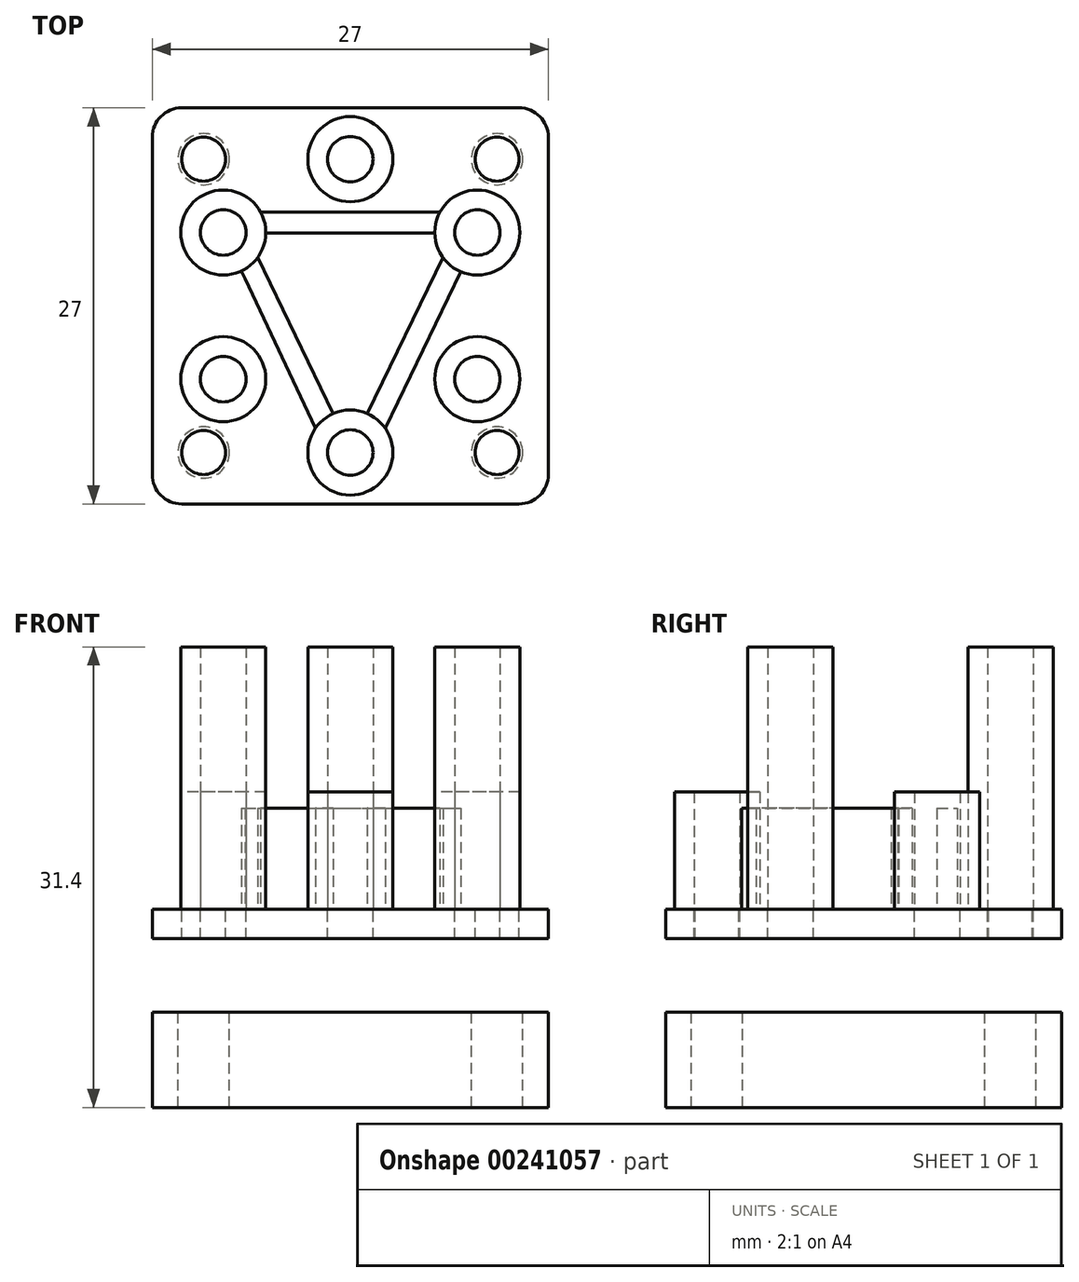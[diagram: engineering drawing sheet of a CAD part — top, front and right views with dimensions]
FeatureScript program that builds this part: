
annotation { "Feature Type Name" : "Feature", "Feature Type Description" : "" }
export const myFeature = defineFeature(function(context is Context, id is Id, definition is map)
    precondition{}
    {
        {
            var Q0;
            Q0=qCreatedBy(makeId("Top.planeOp"),FACE);
            var sketch = newSketch(context, id + "F0", { "sketchPlane" : qUnion([Q0])});
            skLineSegment(sketch, "E0.bottom", {"start": v(-13.5, 13.5) * mm, "end": v(13.5, 13.5) * mm});
            skLineSegment(sketch, "E0.top", {"start": v(-13.5, -13.5) * mm, "end": v(13.5, -13.5) * mm});
            skLineSegment(sketch, "E0.left", {"start": v(-13.5, 13.5) * mm, "end": v(-13.5, -13.5) * mm});
            skLineSegment(sketch, "E0.right", {"start": v(13.5, 13.5) * mm, "end": v(13.5, -13.5) * mm});
            skPoint(sketch, "E1", {"position": v(0, 13.5) * mm});
            skPoint(sketch, "E2", {"position": v(-13.5, 0) * mm});
            skSolve(sketch);
        }
        {
            var Q0;
            Q0=makeQuery(id+"F0.imprint","IMPRINT",FACE,{"disambiguationData":[TD([[makeQuery(id+"F0.imprint","IMPRINT",EDGE,{"derivedFrom":sQuery(id+"F0.wireOp",EDGE,"E0.bottom")}),-1.0]])]});
            extrude(context, id + "F1", {"entities" : qUnion([Q0]), "depth" : 2 * mm});
        }
        {
            var Q0;
            Q0=makeQuery(id+"F1.opExtrude","CAP_FACE",FACE,{"disambiguationData":[OSD([sQuery(id+"F0.wireOp",EDGE,"E0.bottom"),sQuery(id+"F0.wireOp",EDGE,"E0.top"),sQuery(id+"F0.wireOp",EDGE,"E0.left"),sQuery(id+"F0.wireOp",EDGE,"E0.right")])],"isStart":false});
            var sketch = newSketch(context, id + "F2", { "sketchPlane" : qUnion([Q0])});
            skPoint(sketch, "E3", {"position": v(0, 13.5) * mm});
            skPoint(sketch, "E4", {"position": v(-10, 10) * mm});
            skPoint(sketch, "E5", {"position": v(10, 10) * mm});
            skPoint(sketch, "E6", {"position": v(10, -10) * mm});
            skPoint(sketch, "E7", {"position": v(-10, -10) * mm});
            skLineSegment(sketch, "E8", {"start": v(-13.5, 13.5) * mm, "end": v(-10, 13.5) * mm});
            skPoint(sketch, "E9.endSnap0", {"position": v(-11.75, 13.5) * mm});
            skLineSegment(sketch, "E10", {"start": v(-13.5, 13.5) * mm, "end": v(-13.5, 10) * mm});
            skLineSegment(sketch, "E11", {"start": v(13.5, -13.5) * mm, "end": v(13.5, -10) * mm});
            skLineSegment(sketch, "E12", {"start": v(13.5, -13.5) * mm, "end": v(10, -13.5) * mm});
            skCircle(sketch, "E13", {"center": v(-10, 10) * mm, "radius": 1.5 * mm});
            skCircle(sketch, "E14", {"center": v(10, 10) * mm, "radius": 1.5 * mm});
            skCircle(sketch, "E15", {"center": v(-10, -10) * mm, "radius": 1.5 * mm});
            skCircle(sketch, "E16", {"center": v(10, -10) * mm, "radius": 1.5 * mm});
            skLineSegment(sketch, "E17", {"start": v(-10, 10) * mm, "end": v(-10, -10) * mm, "construction": true});
            skLineSegment(sketch, "E18", {"start": v(10, 10) * mm, "end": v(-10, 10) * mm, "construction": true});
            skPoint(sketch, "E19", {"position": v(0, 10) * mm});
            skPoint(sketch, "E20", {"position": v(-10, 0) * mm});
            skSolve(sketch);
        }
        {
            var Q0;
            Q0=makeQuery(id+"F2.imprint","IMPRINT",FACE,{"disambiguationData":[TD([[makeQuery(id+"F2.imprint","IMPRINT",EDGE,{"derivedFrom":sQuery(id+"F2.wireOp",EDGE,"E13")}),1.0]])]});
            var Q1;
            Q1=makeQuery(id+"F2.imprint","IMPRINT",FACE,{"disambiguationData":[TD([[makeQuery(id+"F2.imprint","IMPRINT",EDGE,{"derivedFrom":sQuery(id+"F2.wireOp",EDGE,"E14")}),1.0]])]});
            var Q2;
            Q2=makeQuery(id+"F2.imprint","IMPRINT",FACE,{"disambiguationData":[TD([[makeQuery(id+"F2.imprint","IMPRINT",EDGE,{"derivedFrom":sQuery(id+"F2.wireOp",EDGE,"E16")}),1.0]])]});
            var Q3;
            Q3=makeQuery(id+"F2.imprint","IMPRINT",FACE,{"disambiguationData":[TD([[makeQuery(id+"F2.imprint","IMPRINT",EDGE,{"derivedFrom":sQuery(id+"F2.wireOp",EDGE,"E15")}),1.0]])]});
            extrude(context, id + "F3", {"entities" : qUnion([Q0, Q1, Q2, Q3]), "operationType" : NewBodyOperationType.REMOVE, "oppositeDirection" : true, "depth" : 5 * mm});
        }
        {
            var Q0;
            Q0=makeQuery(id+"F1.opExtrude","SWEPT_EDGE",EDGE,{"disambiguationData":[OSD([sQuery(id+"F0.wireOp",EDGE,"E0.top"),sQuery(id+"F0.wireOp",EDGE,"E0.right")])]});
            var Q1;
            Q1=makeQuery(id+"F1.opExtrude","SWEPT_EDGE",EDGE,{"disambiguationData":[OSD([sQuery(id+"F0.wireOp",EDGE,"E0.bottom"),sQuery(id+"F0.wireOp",EDGE,"E0.left")])]});
            var Q2;
            Q2=makeQuery(id+"F1.opExtrude","SWEPT_EDGE",EDGE,{"disambiguationData":[OSD([sQuery(id+"F0.wireOp",EDGE,"E0.bottom"),sQuery(id+"F0.wireOp",EDGE,"E0.right")])]});
            var Q3;
            Q3=makeQuery(id+"F1.opExtrude","SWEPT_EDGE",EDGE,{"disambiguationData":[OSD([sQuery(id+"F0.wireOp",EDGE,"E0.top"),sQuery(id+"F0.wireOp",EDGE,"E0.left")])]});
            fillet(context, id + "F4", {"entities" : qUnion([Q0, Q1, Q2, Q3]), "radius" : 2 * mm, "tangentPropagation" : true, "allowEdgeOverflow" : false});
        }
        {
            var Q0;
            Q0=makeQuery(id+"F1.opExtrude","CAP_FACE",FACE,{"disambiguationData":[OSD([sQuery(id+"F0.wireOp",EDGE,"E0.bottom"),sQuery(id+"F0.wireOp",EDGE,"E0.top"),sQuery(id+"F0.wireOp",EDGE,"E0.left"),sQuery(id+"F0.wireOp",EDGE,"E0.right")])],"isStart":true});
            var sketch = newSketch(context, id + "F5", { "sketchPlane" : qUnion([Q0])});
            skPoint(sketch, "E21", {"position": v(0, 0) * mm});
            skSolve(sketch);
        }
        {
            var Q0;
            Q0=makeQuery(id+"F1.opExtrude","CAP_FACE",FACE,{"disambiguationData":[OSD([sQuery(id+"F0.wireOp",EDGE,"E0.bottom"),sQuery(id+"F0.wireOp",EDGE,"E0.top"),sQuery(id+"F0.wireOp",EDGE,"E0.left"),sQuery(id+"F0.wireOp",EDGE,"E0.right")])],"isStart":false});
            var sketch = newSketch(context, id + "F6", { "sketchPlane" : qUnion([Q0])});
            skCircle(sketch, "E22.cCircle", {"center": v(0, 0) * mm, "radius": 8.66 * mm, "construction": true});
            skLineSegment(sketch, "E22.0", {"start": v(0, -10) * mm, "end": v(-8.66, -5) * mm});
            skLineSegment(sketch, "E22.1", {"start": v(-8.66, -5) * mm, "end": v(-8.66, 5) * mm});
            skLineSegment(sketch, "E22.2", {"start": v(-8.66, 5) * mm, "end": v(0, 10) * mm});
            skLineSegment(sketch, "E22.3", {"start": v(0, 10) * mm, "end": v(8.66, 5) * mm});
            skLineSegment(sketch, "E22.4", {"start": v(8.66, 5) * mm, "end": v(8.66, -5) * mm});
            skLineSegment(sketch, "E22.5", {"start": v(8.66, -5) * mm, "end": v(0, -10) * mm});
            skPoint(sketch, "E22.0.midPoint", {"position": v(-4.33, -7.5) * mm});
            skPoint(sketch, "E23", {"position": v(0, 10) * mm});
            skPoint(sketch, "E24", {"position": v(0, -10) * mm});
            skPoint(sketch, "E25", {"position": v(-8.66, 0) * mm});
            skCircle(sketch, "E26", {"center": v(0, 10) * mm, "radius": 1.55 * mm});
            skCircle(sketch, "E27", {"center": v(-8.66, -5) * mm, "radius": 1.55 * mm});
            skCircle(sketch, "E28", {"center": v(8.66, -5) * mm, "radius": 1.55 * mm});
            skCircle(sketch, "E29", {"center": v(-8.66, 5) * mm, "radius": 1.55 * mm});
            skCircle(sketch, "E30", {"center": v(8.66, 5) * mm, "radius": 1.55 * mm});
            skCircle(sketch, "E31", {"center": v(0, -10) * mm, "radius": 1.55 * mm});
            skCircle(sketch, "E32", {"center": v(-8.66, 5) * mm, "radius": 2.9 * mm});
            skCircle(sketch, "E33", {"center": v(-8.66, -5) * mm, "radius": 2.9 * mm});
            skCircle(sketch, "E34", {"center": v(0, -10) * mm, "radius": 2.9 * mm});
            skCircle(sketch, "E35", {"center": v(8.66, -5) * mm, "radius": 2.9 * mm});
            skCircle(sketch, "E36", {"center": v(8.66, 5) * mm, "radius": 2.9 * mm});
            skCircle(sketch, "E37", {"center": v(0, 10) * mm, "radius": 2.9 * mm});
            skPoint(sketch, "E38", {"position": v(-5.76, 4.98) * mm});
            skPoint(sketch, "E39", {"position": v(5.76, 4.98) * mm});
            skPoint(sketch, "E40", {"position": v(46.87, -20.06) * mm});
            skLineSegment(sketch, "E41", {"start": v(-5.76, 4.98) * mm, "end": v(5.76, 4.98) * mm});
            skPoint(sketch, "E42", {"position": v(-1.16, -7.34) * mm});
            skPoint(sketch, "E43", {"position": v(1.16, -7.34) * mm});
            skPoint(sketch, "E44", {"position": v(-6.3, 3.3) * mm});
            skPoint(sketch, "E45", {"position": v(6.3, 3.3) * mm});
            skLineSegment(sketch, "E46", {"start": v(-6.3, 3.3) * mm, "end": v(-1.16, -7.34) * mm});
            skLineSegment(sketch, "E47", {"start": v(1.16, -7.34) * mm, "end": v(6.3, 3.3) * mm});
            skPoint(sketch, "E48", {"position": v(-7.43, 2.37) * mm});
            skLineSegment(sketch, "E49", {"start": v(-7.43, 2.37) * mm, "end": v(-7.18, 1.86) * mm});
            skLineSegment(sketch, "E50", {"start": v(-7.18, 1.86) * mm, "end": v(-2.39, -8.35) * mm});
            skLineSegment(sketch, "E51", {"start": v(0, 6.38) * mm, "end": v(6.1, 6.38) * mm});
            skLineSegment(sketch, "E52", {"start": v(0, 6.38) * mm, "end": v(-6.1, 6.38) * mm});
            skPoint(sketch, "E53", {"position": v(2.37, -8.33) * mm});
            skLineSegment(sketch, "E54", {"start": v(2.37, -8.33) * mm, "end": v(7.53, 2.33) * mm});
            skSolve(sketch);
        }
        {
            var Q0;
            {var subQ0=sQuery(id+"F6.wireOp",EDGE,"E37");var subQ1=sQuery(id+"F6.wireOp",EDGE,"E22.2");var subQ2=makeQuery(id+"F6.imprint","INTERSECT",VERTEX,{"derivedFrom":[subQ1,subQ0]});Q0=makeQuery(id+"F6.imprint","IMPRINT",FACE,{"disambiguationData":[TD([[makeQuery(id+"F6.imprint","IMPRINT",EDGE,{"disambiguationData":[TD([[subQ2,-1.0]])],"derivedFrom":subQ1}),1.0]])]});}
            var Q1;
            {var subQ0=sQuery(id+"F6.wireOp",EDGE,"E37");var subQ1=sQuery(id+"F6.wireOp",EDGE,"E22.2");var subQ2=makeQuery(id+"F6.imprint","INTERSECT",VERTEX,{"derivedFrom":[subQ1,subQ0]});Q1=makeQuery(id+"F6.imprint","IMPRINT",FACE,{"disambiguationData":[TD([[makeQuery(id+"F6.imprint","IMPRINT",EDGE,{"disambiguationData":[TD([[subQ2,-1.0]])],"derivedFrom":subQ1}),-1.0]])]});}
            var Q2;
            {var subQ0=sQuery(id+"F6.wireOp",EDGE,"E35");var subQ1=sQuery(id+"F6.wireOp",EDGE,"E22.4");var subQ2=makeQuery(id+"F6.imprint","INTERSECT",VERTEX,{"derivedFrom":[subQ1,subQ0]});Q2=makeQuery(id+"F6.imprint","IMPRINT",FACE,{"disambiguationData":[TD([[makeQuery(id+"F6.imprint","IMPRINT",EDGE,{"disambiguationData":[TD([[subQ2,-1.0]])],"derivedFrom":subQ1}),1.0]])]});}
            var Q3;
            {var subQ0=sQuery(id+"F6.wireOp",EDGE,"E35");var subQ1=sQuery(id+"F6.wireOp",EDGE,"E22.4");var subQ2=makeQuery(id+"F6.imprint","INTERSECT",VERTEX,{"derivedFrom":[subQ1,subQ0]});Q3=makeQuery(id+"F6.imprint","IMPRINT",FACE,{"disambiguationData":[TD([[makeQuery(id+"F6.imprint","IMPRINT",EDGE,{"disambiguationData":[TD([[subQ2,-1.0]])],"derivedFrom":subQ1}),-1.0]])]});}
            var Q4;
            {var subQ0=sQuery(id+"F6.wireOp",EDGE,"E33");var subQ1=sQuery(id+"F6.wireOp",EDGE,"E22.0");var subQ2=makeQuery(id+"F6.imprint","INTERSECT",VERTEX,{"derivedFrom":[subQ1,subQ0]});Q4=makeQuery(id+"F6.imprint","IMPRINT",FACE,{"disambiguationData":[TD([[makeQuery(id+"F6.imprint","IMPRINT",EDGE,{"disambiguationData":[TD([[subQ2,-1.0]])],"derivedFrom":subQ1}),1.0]])]});}
            var Q5;
            {var subQ0=sQuery(id+"F6.wireOp",EDGE,"E33");var subQ1=sQuery(id+"F6.wireOp",EDGE,"E22.0");var subQ2=makeQuery(id+"F6.imprint","INTERSECT",VERTEX,{"derivedFrom":[subQ1,subQ0]});Q5=makeQuery(id+"F6.imprint","IMPRINT",FACE,{"disambiguationData":[TD([[makeQuery(id+"F6.imprint","IMPRINT",EDGE,{"disambiguationData":[TD([[subQ2,-1.0]])],"derivedFrom":subQ1}),-1.0]])]});}
            extrude(context, id + "F7", {"entities" : qUnion([Q0, Q1, Q2, Q3, Q4, Q5]), "depth" : 17.9 * mm});
        }
        {
            var Q0;
            {var subQ0=sQuery(id+"F6.wireOp",EDGE,"E32");var subQ1=sQuery(id+"F6.wireOp",EDGE,"E22.1");var subQ2=makeQuery(id+"F6.imprint","INTERSECT",VERTEX,{"derivedFrom":[subQ1,subQ0]});Q0=makeQuery(id+"F6.imprint","IMPRINT",FACE,{"disambiguationData":[TD([[makeQuery(id+"F6.imprint","IMPRINT",EDGE,{"disambiguationData":[TD([[subQ2,-1.0]])],"derivedFrom":subQ1}),1.0]])]});}
            var Q1;
            {var subQ0=sQuery(id+"F6.wireOp",EDGE,"E32");var subQ1=sQuery(id+"F6.wireOp",EDGE,"E22.1");var subQ2=makeQuery(id+"F6.imprint","INTERSECT",VERTEX,{"derivedFrom":[subQ1,subQ0]});Q1=makeQuery(id+"F6.imprint","IMPRINT",FACE,{"disambiguationData":[TD([[makeQuery(id+"F6.imprint","IMPRINT",EDGE,{"disambiguationData":[TD([[subQ2,-1.0]])],"derivedFrom":subQ1}),-1.0]])]});}
            var Q2;
            {var subQ0=sQuery(id+"F6.wireOp",EDGE,"E36");var subQ1=sQuery(id+"F6.wireOp",EDGE,"E22.3");var subQ2=makeQuery(id+"F6.imprint","INTERSECT",VERTEX,{"derivedFrom":[subQ1,subQ0]});Q2=makeQuery(id+"F6.imprint","IMPRINT",FACE,{"disambiguationData":[TD([[makeQuery(id+"F6.imprint","IMPRINT",EDGE,{"disambiguationData":[TD([[subQ2,-1.0]])],"derivedFrom":subQ1}),-1.0]])]});}
            var Q3;
            {var subQ0=sQuery(id+"F6.wireOp",EDGE,"E36");var subQ1=sQuery(id+"F6.wireOp",EDGE,"E22.3");var subQ2=makeQuery(id+"F6.imprint","INTERSECT",VERTEX,{"derivedFrom":[subQ1,subQ0]});Q3=makeQuery(id+"F6.imprint","IMPRINT",FACE,{"disambiguationData":[TD([[makeQuery(id+"F6.imprint","IMPRINT",EDGE,{"disambiguationData":[TD([[subQ2,-1.0]])],"derivedFrom":subQ1}),1.0]])]});}
            var Q4;
            {var subQ0=sQuery(id+"F6.wireOp",EDGE,"E31");var subQ1=sQuery(id+"F6.wireOp",EDGE,"E22.0");var subQ2=makeQuery(id+"F6.imprint","INTERSECT",VERTEX,{"derivedFrom":[subQ1,subQ0]});Q4=makeQuery(id+"F6.imprint","IMPRINT",FACE,{"disambiguationData":[TD([[makeQuery(id+"F6.imprint","IMPRINT",EDGE,{"disambiguationData":[TD([[subQ2,-1.0]])],"derivedFrom":subQ1}),1.0]])]});}
            var Q5;
            {var subQ0=sQuery(id+"F6.wireOp",EDGE,"E31");var subQ1=sQuery(id+"F6.wireOp",EDGE,"E22.0");var subQ2=makeQuery(id+"F6.imprint","INTERSECT",VERTEX,{"derivedFrom":[subQ1,subQ0]});Q5=makeQuery(id+"F6.imprint","IMPRINT",FACE,{"disambiguationData":[TD([[makeQuery(id+"F6.imprint","IMPRINT",EDGE,{"disambiguationData":[TD([[subQ2,-1.0]])],"derivedFrom":subQ1}),-1.0]])]});}
            extrude(context, id + "F8", {"entities" : qUnion([Q0, Q1, Q2, Q3, Q4, Q5]), "depth" : 8 * mm});
        }
        {
            var Q0;
            {var subQ0=sQuery(id+"F6.wireOp",EDGE,"E22.5");var subQ1=sQuery(id+"F6.wireOp",EDGE,"E22.4");var subQ2=makeQuery(id+"F6.imprint","INTERSECT",VERTEX,{"derivedFrom":[subQ1,subQ0]});Q0=makeQuery(id+"F6.imprint","IMPRINT",FACE,{"disambiguationData":[TD([[makeQuery(id+"F6.imprint","IMPRINT",EDGE,{"disambiguationData":[TD([[subQ2,1.0]])],"derivedFrom":subQ1}),1.0]])]});}
            var Q1;
            {var subQ0=sQuery(id+"F6.wireOp",EDGE,"E22.5");var subQ1=sQuery(id+"F6.wireOp",EDGE,"E22.4");var subQ2=makeQuery(id+"F6.imprint","INTERSECT",VERTEX,{"derivedFrom":[subQ1,subQ0]});Q1=makeQuery(id+"F6.imprint","IMPRINT",FACE,{"disambiguationData":[TD([[makeQuery(id+"F6.imprint","IMPRINT",EDGE,{"disambiguationData":[TD([[subQ2,1.0]])],"derivedFrom":subQ1}),-1.0]])]});}
            var Q2;
            {var subQ0=sQuery(id+"F6.wireOp",EDGE,"E22.3");var subQ1=sQuery(id+"F6.wireOp",EDGE,"E22.2");var subQ2=makeQuery(id+"F6.imprint","INTERSECT",VERTEX,{"derivedFrom":[subQ1,subQ0]});Q2=makeQuery(id+"F6.imprint","IMPRINT",FACE,{"disambiguationData":[TD([[makeQuery(id+"F6.imprint","IMPRINT",EDGE,{"disambiguationData":[TD([[subQ2,1.0]])],"derivedFrom":subQ1}),1.0]])]});}
            var Q3;
            {var subQ0=sQuery(id+"F6.wireOp",EDGE,"E22.3");var subQ1=sQuery(id+"F6.wireOp",EDGE,"E22.2");var subQ2=makeQuery(id+"F6.imprint","INTERSECT",VERTEX,{"derivedFrom":[subQ1,subQ0]});Q3=makeQuery(id+"F6.imprint","IMPRINT",FACE,{"disambiguationData":[TD([[makeQuery(id+"F6.imprint","IMPRINT",EDGE,{"disambiguationData":[TD([[subQ2,1.0]])],"derivedFrom":subQ1}),-1.0]])]});}
            var Q4;
            {var subQ0=sQuery(id+"F6.wireOp",EDGE,"E22.4");var subQ1=sQuery(id+"F6.wireOp",EDGE,"E22.3");var subQ2=makeQuery(id+"F6.imprint","INTERSECT",VERTEX,{"derivedFrom":[subQ1,subQ0]});Q4=makeQuery(id+"F6.imprint","IMPRINT",FACE,{"disambiguationData":[TD([[makeQuery(id+"F6.imprint","IMPRINT",EDGE,{"disambiguationData":[TD([[subQ2,1.0]])],"derivedFrom":subQ1}),-1.0]])]});}
            var Q5;
            {var subQ0=sQuery(id+"F6.wireOp",EDGE,"E22.4");var subQ1=sQuery(id+"F6.wireOp",EDGE,"E22.3");var subQ2=makeQuery(id+"F6.imprint","INTERSECT",VERTEX,{"derivedFrom":[subQ1,subQ0]});Q5=makeQuery(id+"F6.imprint","IMPRINT",FACE,{"disambiguationData":[TD([[makeQuery(id+"F6.imprint","IMPRINT",EDGE,{"disambiguationData":[TD([[subQ2,1.0]])],"derivedFrom":subQ1}),1.0]])]});}
            var Q6;
            {var subQ0=sQuery(id+"F6.wireOp",EDGE,"E22.2");var subQ1=sQuery(id+"F6.wireOp",EDGE,"E22.1");var subQ2=makeQuery(id+"F6.imprint","INTERSECT",VERTEX,{"derivedFrom":[subQ1,subQ0]});Q6=makeQuery(id+"F6.imprint","IMPRINT",FACE,{"disambiguationData":[TD([[makeQuery(id+"F6.imprint","IMPRINT",EDGE,{"disambiguationData":[TD([[subQ2,1.0]])],"derivedFrom":subQ1}),1.0]])]});}
            var Q7;
            {var subQ0=sQuery(id+"F6.wireOp",EDGE,"E22.2");var subQ1=sQuery(id+"F6.wireOp",EDGE,"E22.1");var subQ2=makeQuery(id+"F6.imprint","INTERSECT",VERTEX,{"derivedFrom":[subQ1,subQ0]});Q7=makeQuery(id+"F6.imprint","IMPRINT",FACE,{"disambiguationData":[TD([[makeQuery(id+"F6.imprint","IMPRINT",EDGE,{"disambiguationData":[TD([[subQ2,1.0]])],"derivedFrom":subQ1}),-1.0]])]});}
            var Q8;
            {var subQ0=sQuery(id+"F6.wireOp",EDGE,"E22.1");var subQ1=sQuery(id+"F6.wireOp",EDGE,"E22.0");var subQ2=makeQuery(id+"F6.imprint","INTERSECT",VERTEX,{"derivedFrom":[subQ1,subQ0]});Q8=makeQuery(id+"F6.imprint","IMPRINT",FACE,{"disambiguationData":[TD([[makeQuery(id+"F6.imprint","IMPRINT",EDGE,{"disambiguationData":[TD([[subQ2,1.0]])],"derivedFrom":subQ1}),1.0]])]});}
            var Q9;
            {var subQ0=sQuery(id+"F6.wireOp",EDGE,"E22.1");var subQ1=sQuery(id+"F6.wireOp",EDGE,"E22.0");var subQ2=makeQuery(id+"F6.imprint","INTERSECT",VERTEX,{"derivedFrom":[subQ1,subQ0]});Q9=makeQuery(id+"F6.imprint","IMPRINT",FACE,{"disambiguationData":[TD([[makeQuery(id+"F6.imprint","IMPRINT",EDGE,{"disambiguationData":[TD([[subQ2,1.0]])],"derivedFrom":subQ1}),-1.0]])]});}
            var Q10;
            {var subQ0=sQuery(id+"F6.wireOp",EDGE,"E22.5");var subQ1=sQuery(id+"F6.wireOp",EDGE,"E22.0");var subQ2=makeQuery(id+"F6.imprint","INTERSECT",VERTEX,{"derivedFrom":[subQ1,subQ0]});Q10=makeQuery(id+"F6.imprint","IMPRINT",FACE,{"disambiguationData":[TD([[makeQuery(id+"F6.imprint","IMPRINT",EDGE,{"disambiguationData":[TD([[subQ2,-1.0]])],"derivedFrom":subQ1}),-1.0]])]});}
            var Q11;
            {var subQ0=sQuery(id+"F6.wireOp",EDGE,"E22.5");var subQ1=sQuery(id+"F6.wireOp",EDGE,"E22.0");var subQ2=makeQuery(id+"F6.imprint","INTERSECT",VERTEX,{"derivedFrom":[subQ1,subQ0]});Q11=makeQuery(id+"F6.imprint","IMPRINT",FACE,{"disambiguationData":[TD([[makeQuery(id+"F6.imprint","IMPRINT",EDGE,{"disambiguationData":[TD([[subQ2,-1.0]])],"derivedFrom":subQ1}),1.0]])]});}
            extrude(context, id + "F9", {"entities" : qUnion([Q0, Q1, Q2, Q3, Q4, Q5, Q6, Q7, Q8, Q9, Q10, Q11]), "operationType" : NewBodyOperationType.REMOVE, "oppositeDirection" : true, "depth" : 2 * mm});
        }
        {
            var Q0;
            Q0=sQuery(id+"F6.wireOp",EDGE,"E41");
            var Q1;
            Q1=sQuery(id+"F6.wireOp",EDGE,"11q2PArW-vFP4-Kt5A-4JWQ-UoNziAoK3fkI");
            var Q2;
            Q2=sQuery(id+"F6.wireOp",EDGE,"hljJpvWc-3PZt-Nu9d-bWFU-MsNhOqhUzWAJ");
            var Q3;
            Q3=sQuery(id+"F6.wireOp",EDGE,"1hEFrna0-KamV-VUdG-DbXB-W5naauOhw6Zd");
            extrude(context, id + "F10", {"bodyType" : ToolBodyType.SURFACE, "surfaceEntities" : qUnion([Q0, Q1, Q2, Q3]), "depth" : 6.9 * mm});
        }
        {
            var Q0;
            {var subQ1=sQuery(id+"F6.wireOp",EDGE,"E46");Q0=makeQuery(id+"F6.imprint","IMPRINT",FACE,{"disambiguationData":[TD([[makeQuery(id+"F6.imprint","IMPRINT",EDGE,{"derivedFrom":subQ1}),-1.0]])]});}
            var Q1;
            {var subQ1=sQuery(id+"F6.wireOp",EDGE,"E41");Q1=makeQuery(id+"F6.imprint","IMPRINT",FACE,{"disambiguationData":[TD([[makeQuery(id+"F6.imprint","IMPRINT",EDGE,{"derivedFrom":subQ1}),1.0]])]});}
            var Q2;
            {var subQ0=sQuery(id+"F6.wireOp",EDGE,"E47");Q2=makeQuery(id+"F6.imprint","IMPRINT",FACE,{"disambiguationData":[TD([[makeQuery(id+"F6.imprint","IMPRINT",EDGE,{"derivedFrom":subQ0}),-1.0]])]});}
            extrude(context, id + "F11", {"entities" : qUnion([Q0, Q1, Q2]), "depth" : 6.9 * mm});
        }
        {
            var Q0;
            Q0=qCreatedBy(makeId("Top.planeOp"),FACE);
            cPlane(context, id + "F12", {"entities" : qUnion([Q0]), "cplaneType" : CPlaneType.OFFSET, "offset" : 5 * mm, "oppositeDirection" : true, "width" : 150 * mm, "height" : 150 * mm});
        }
        {
            var Q0;
            Q0=qCreatedBy(id+"F12.planeOp",FACE);
            var sketch = newSketch(context, id + "F13", { "sketchPlane" : qUnion([Q0])});
            skLineSegment(sketch, "E55.0.0", {"start": v(11.5, -13.5) * mm, "end": v(-11.5, -13.5) * mm});
            skArc(sketch, "E55.0.1", {"start": v(-11.5, -13.5) * mm, "mid": v(-12.91, -12.91) * mm, "end": v(-13.5, -11.5) * mm});
            skLineSegment(sketch, "E55.0.2", {"start": v(-13.5, -11.5) * mm, "end": v(-13.5, 11.5) * mm});
            skArc(sketch, "E55.0.3", {"start": v(-13.5, 11.5) * mm, "mid": v(-12.91, 12.91) * mm, "end": v(-11.5, 13.5) * mm});
            skLineSegment(sketch, "E55.0.4", {"start": v(-11.5, 13.5) * mm, "end": v(11.5, 13.5) * mm});
            skArc(sketch, "E55.0.5", {"start": v(11.5, 13.5) * mm, "mid": v(12.91, 12.91) * mm, "end": v(13.5, 11.5) * mm});
            skLineSegment(sketch, "E55.0.6", {"start": v(13.5, 11.5) * mm, "end": v(13.5, -11.5) * mm});
            skArc(sketch, "E55.0.7", {"start": v(13.5, -11.5) * mm, "mid": v(12.91, -12.91) * mm, "end": v(11.5, -13.5) * mm});
            skCircle(sketch, "E56.0", {"center": v(-10, -10) * mm, "radius": 1.5 * mm, "construction": true});
            skCircle(sketch, "E57.0.0", {"center": v(10, -10) * mm, "radius": 1.5 * mm, "construction": true});
            skCircle(sketch, "E58.0", {"center": v(-10, 10) * mm, "radius": 1.5 * mm, "construction": true});
            skCircle(sketch, "E59.0", {"center": v(10, 10) * mm, "radius": 1.5 * mm, "construction": true});
            skCircle(sketch, "E60", {"center": v(-10, -10) * mm, "radius": 1.75 * mm});
            skCircle(sketch, "E61.MirrorC", {"center": v(10, -10) * mm, "radius": 1.75 * mm});
            skCircle(sketch, "E62.MirrorC", {"center": v(-10, 10) * mm, "radius": 1.75 * mm});
            skCircle(sketch, "E63.MirrorC", {"center": v(10, 10) * mm, "radius": 1.75 * mm});
            skSolve(sketch);
        }
        {
            var Q0;
            Q0=makeQuery(id+"F13.imprint","IMPRINT",FACE,{"disambiguationData":[TD([[makeQuery(id+"F13.imprint","IMPRINT",EDGE,{"derivedFrom":sQuery(id+"F13.wireOp",EDGE,"E55.0.0")}),-1.0]])]});
            extrude(context, id + "F14", {"entities" : qUnion([Q0]), "oppositeDirection" : true, "depth" : 6.5 * mm});
        }
        {
            var Q0;
            Q0=makeQuery(id+"F10.opExtrude","SWEPT_BODY",BODY,{"disambiguationData":[OSD([sQuery(id+"F6.wireOp",EDGE,"E41")])]});
            deleteBodies(context, id + "F15", {"entities" : qUnion([Q0])});
        }
    });
